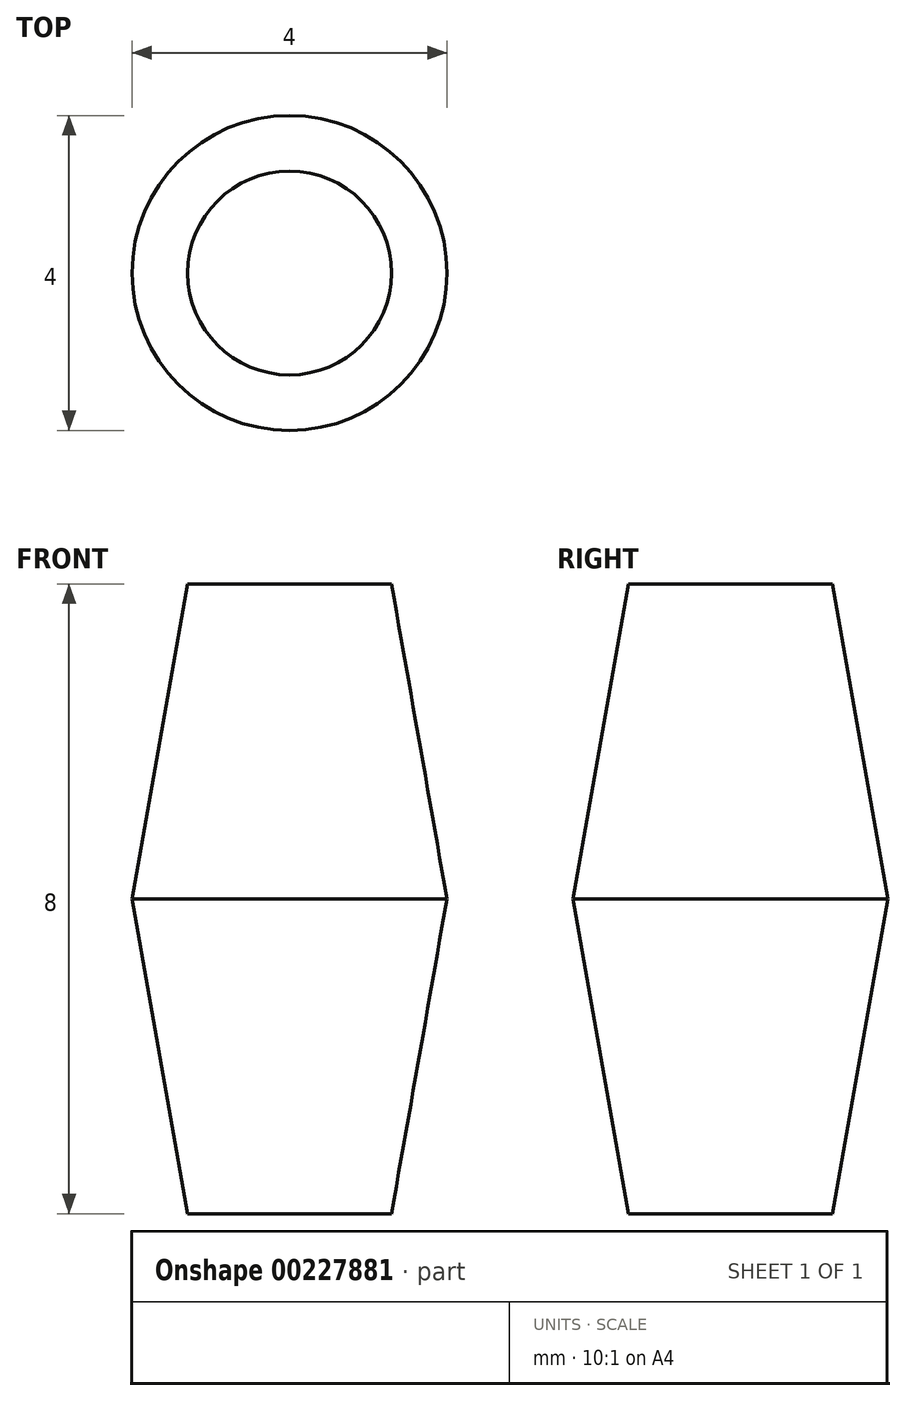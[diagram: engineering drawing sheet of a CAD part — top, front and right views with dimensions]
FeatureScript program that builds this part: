
annotation { "Feature Type Name" : "Feature", "Feature Type Description" : "" }
export const myFeature = defineFeature(function(context is Context, id is Id, definition is map)
    precondition{}
    {
        {
            var Q0;
            Q0=qCreatedBy(makeId("Top.planeOp"),FACE);
            var sketch = newSketch(context, id + "F0", { "sketchPlane" : qUnion([Q0])});
            skCircle(sketch, "E0", {"center": v(0, 0) * mm, "radius": 2 * mm});
            skSolve(sketch);
        }
        {
            var Q0;
            Q0=qSketchRegion(id+"F0",true);
            extrude(context, id + "F1", {"entities" : qUnion([Q0]), "depth" : 4 * mm, "hasDraft" : true, "draftAngle" : 10 * degree, "draftPullDirection" : true, "hasSecondDirection" : true, "secondDirectionOppositeDirection" : true, "secondDirectionDepth" : 4 * mm, "hasSecondDirectionDraft" : true, "secondDirectionDraftAngle" : 10 * degree, "secondDirectionDraftPullDirection" : true});
        }
    });
